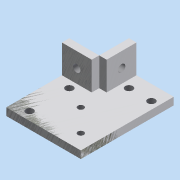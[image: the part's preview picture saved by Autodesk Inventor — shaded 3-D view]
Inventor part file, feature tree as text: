
AUTODESK INVENTOR PART (.ipt)
format: ipt  version: 2015 (Build 190159000, 159)  size: 155,136 bytes
history: native  units: mm
features: sketch x6, hole x5, extrude x2
ambient origin geometry x8: Origin, YZ Plane, XZ Plane, XY Plane, X Axis, Y Axis, Z Axis, Center Point
bodies: Solid1 (feature_tree)
feature tree (13):
  sketch  "Sketch1"  dims[d0=30.0mm d16=42.3mm]
  extrude  "Extrusion2"  Depth=42.3mm
  hole  "Hole3"  [1 undecoded]
  hole  "Hole4"  [1 undecoded]
  hole  "Hole5"  [1 undecoded]
  extrude  "Extrusion3"  Depth=25.0mm
  hole  "Hole6"  [1 undecoded]
  hole  "Hole7"  [1 undecoded]
  sketch  "Sketch2"  dims[d21=20.0mm d22=20.0mm]
  sketch  "Sketch3"  dims[d40=5.0mm d41=0.0mm]
  sketch  "Sketch4"  dims[d42=5.0mm d43=6.0mm d44=4.0mm d45=2.0mm d46=90.0deg d47=8.0mm d48=20.594885mm d49=30.0mm]
  sketch  "Sketch5"  dims[d50=5.0mm d51=10.0mm]
  sketch  "Sketch6"  dims[d52=10.0mm d53=4.0mm d54=6.0mm d55=4.0mm d56=2.0mm d57=90.0deg d58=8.0mm d59=20.594885mm d60=25.0mm d61=25.0mm d62=4.0mm d63=6.0mm d64=4.0mm d65=2.0mm d66=90.0deg d67=8.0mm d68=20.594885mm d69=10.0mm d70=10.0mm d71=10.0mm d72=5.0mm d73=5.0mm d74=19.0mm d75=0.0mm d76=10.0mm d77=10.0mm d78=5.0mm d79=6.0mm d80=4.0mm d81=2.0mm d82=90.0deg d83=8.0mm d84=20.594885mm d85=10.0mm d86=10.0mm d87=5.0mm d88=6.0mm d89=4.0mm d90=2.0mm d91=90.0deg d92=8.0mm d93=20.594885mm]
note: 5 required parameter values undecoded (feature->parameter linkage not recoverable at this tier; creation-order binding heuristic only, values carry confidence <= 0.55)
